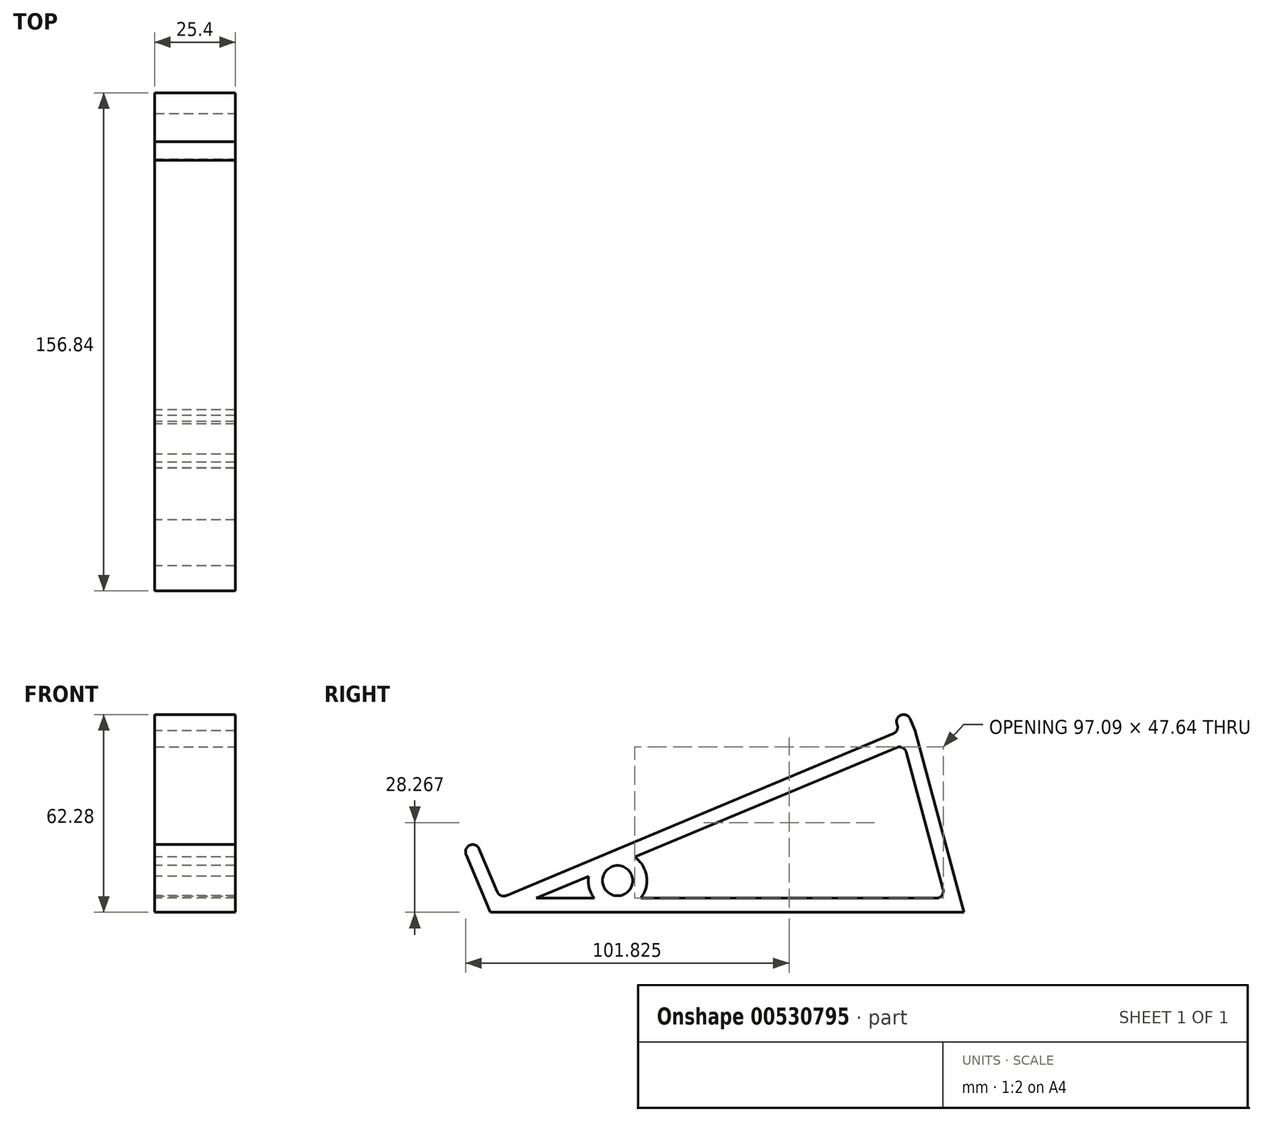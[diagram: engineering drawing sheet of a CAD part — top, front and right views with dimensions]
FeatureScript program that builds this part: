
annotation { "Feature Type Name" : "Feature", "Feature Type Description" : "" }
export const myFeature = defineFeature(function(context is Context, id is Id, definition is map)
    precondition{}
    {
        {
            assignVariable(context, id + "F0", {"name" : "width", "anyValue" : 25.4 * mm});
        }
        {
            assignVariable(context, id + "F1", {"name" : "thickness", "anyValue" : 4.44 * mm});
        }
        {
            var Q0;
            Q0=qCreatedBy(makeId("Right.planeOp"),FACE);
            var sketch = newSketch(context, id + "F2", { "sketchPlane" : qUnion([Q0])});
            skLineSegment(sketch, "E0", {"start": v(-20.13, 57.15) * mm, "end": v(-146.07, 4.45) * mm});
            skLineSegment(sketch, "E1", {"start": v(-146.07, 4.45) * mm, "end": v(-153.43, 22.02) * mm});
            skLineSegment(sketch, "E2", {"start": v(-153.43, 22.02) * mm, "end": v(-157.53, 20.3) * mm});
            skLineSegment(sketch, "E3", {"start": v(-157.53, 20.3) * mm, "end": v(-149.03, 0) * mm});
            skLineSegment(sketch, "E4", {"start": v(-149.03, 0) * mm, "end": v(0, 0) * mm});
            skLineSegment(sketch, "E5", {"start": v(-17.75, 62.97) * mm, "end": v(-21.85, 61.25) * mm});
            skLineSegment(sketch, "E6", {"start": v(-21.85, 61.25) * mm, "end": v(-20.13, 57.15) * mm});
            skCircle(sketch, "E7", {"center": v(-109, 9.98) * mm, "radius": 4.76 * mm});
            skLineSegment(sketch, "E8", {"start": v(-109, 19.96) * mm, "end": v(-109, 0) * mm, "construction": true});
            skLineSegment(sketch, "E9", {"start": v(0, 0) * mm, "end": v(-15.31, 57.15) * mm});
            skLineSegment(sketch, "E10", {"start": v(-15.31, 57.15) * mm, "end": v(-17.75, 62.97) * mm});
            skSolve(sketch);
        }
        {
            var Q0;
            Q0=makeQuery(id+"F2.imprint","IMPRINT",FACE,{"disambiguationData":[TD([[makeQuery(id+"F2.imprint","IMPRINT",EDGE,{"derivedFrom":sQuery(id+"F2.wireOp",EDGE,"E0")}),1.0]])]});
            extrude(context, id + "F3", {"entities" : qUnion([Q0]), "endBound" : BoundingType.SYMMETRIC, "depth" : getVariable(context, 'width'), "offsetDistance" : 25.4 * mm});
        }
        {
            var Q0;
            Q0=makeQuery(id+"F3.opExtrude","CAP_FACE",FACE,{"disambiguationData":[OSD([sQuery(id+"F2.wireOp",EDGE,"E0"),sQuery(id+"F2.wireOp",EDGE,"E1"),sQuery(id+"F2.wireOp",EDGE,"E2"),sQuery(id+"F2.wireOp",EDGE,"E3"),sQuery(id+"F2.wireOp",EDGE,"E4"),sQuery(id+"F2.wireOp",EDGE,"sQ11OlKh-m7nL-uf8o-I6ZN-qrxeiSYvcrfF"),sQuery(id+"F2.wireOp",EDGE,"E5"),sQuery(id+"F2.wireOp",EDGE,"E6"),sQuery(id+"F2.wireOp",EDGE,"E7")])],"isStart":false});
            var Q1;
            Q1=makeQuery(id+"F3.opExtrude","CAP_FACE",FACE,{"disambiguationData":[OSD([sQuery(id+"F2.wireOp",EDGE,"E0"),sQuery(id+"F2.wireOp",EDGE,"E1"),sQuery(id+"F2.wireOp",EDGE,"E2"),sQuery(id+"F2.wireOp",EDGE,"E3"),sQuery(id+"F2.wireOp",EDGE,"E4"),sQuery(id+"F2.wireOp",EDGE,"sQ11OlKh-m7nL-uf8o-I6ZN-qrxeiSYvcrfF"),sQuery(id+"F2.wireOp",EDGE,"E5"),sQuery(id+"F2.wireOp",EDGE,"E6"),sQuery(id+"F2.wireOp",EDGE,"E7")])],"isStart":true});
            shell(context, id + "F4", {"entities" : qUnion([Q0, Q1]), "thickness" : getVariable(context, 'thickness')});
        }
        {
            var Q0;
            Q0=makeQuery(id+"F3.opExtrude","SWEPT_EDGE",EDGE,{"disambiguationData":[OSD([sQuery(id+"F2.wireOp",EDGE,"E0"),sQuery(id+"F2.wireOp",EDGE,"E6")])]});
            var Q1;
            Q1=makeQuery(id+"F3.opExtrude","SWEPT_EDGE",EDGE,{"disambiguationData":[OSD([sQuery(id+"F2.wireOp",EDGE,"E0"),sQuery(id+"F2.wireOp",EDGE,"E1")])]});
            var Q2;
            Q2=makeQuery(id+"F3.opExtrude","SWEPT_EDGE",EDGE,{"disambiguationData":[OSD([sQuery(id+"F2.wireOp",EDGE,"E1"),sQuery(id+"F2.wireOp",EDGE,"E2")])]});
            var Q3;
            Q3=makeQuery(id+"F3.opExtrude","SWEPT_EDGE",EDGE,{"disambiguationData":[OSD([sQuery(id+"F2.wireOp",EDGE,"E2"),sQuery(id+"F2.wireOp",EDGE,"E3")])]});
            var Q4;
            Q4=makeQuery(id+"F3.opExtrude","SWEPT_EDGE",EDGE,{"disambiguationData":[OSD([sQuery(id+"F2.wireOp",EDGE,"E5"),sQuery(id+"F2.wireOp",EDGE,"E10")])]});
            var Q5;
            Q5=makeQuery(id+"F3.opExtrude","SWEPT_EDGE",EDGE,{"disambiguationData":[OSD([sQuery(id+"F2.wireOp",EDGE,"E5"),sQuery(id+"F2.wireOp",EDGE,"E6")])]});
            var Q6;
            Q6=makeQuery(id+"F4.opShell","TWEAK_EDGE",EDGE,{"derivedFrom":[makeQuery(id+"F3.opExtrude","SWEPT_FACE",FACE,{"disambiguationData":[OSD([sQuery(id+"F2.wireOp",EDGE,"E0")])]}),makeQuery(id+"F3.opExtrude","SWEPT_FACE",FACE,{"disambiguationData":[OSD([sQuery(id+"F2.wireOp",EDGE,"E9")])]})]});
            var Q7;
            Q7=makeQuery(id+"F4.opShell","OFFSET_EDGE",EDGE,{"disambiguationData":[OSD([sQuery(id+"F2.wireOp",EDGE,"E4"),sQuery(id+"F2.wireOp",EDGE,"E9")])]});
            fillet(context, id + "F5", {"entities" : qUnion([Q0, Q1, Q2, Q3, Q4, Q5, Q6, Q7]), "radius" : getVariable(context, 'thickness') / 2, "tangentPropagation" : true, "allowEdgeOverflow" : false});
        }
    });
